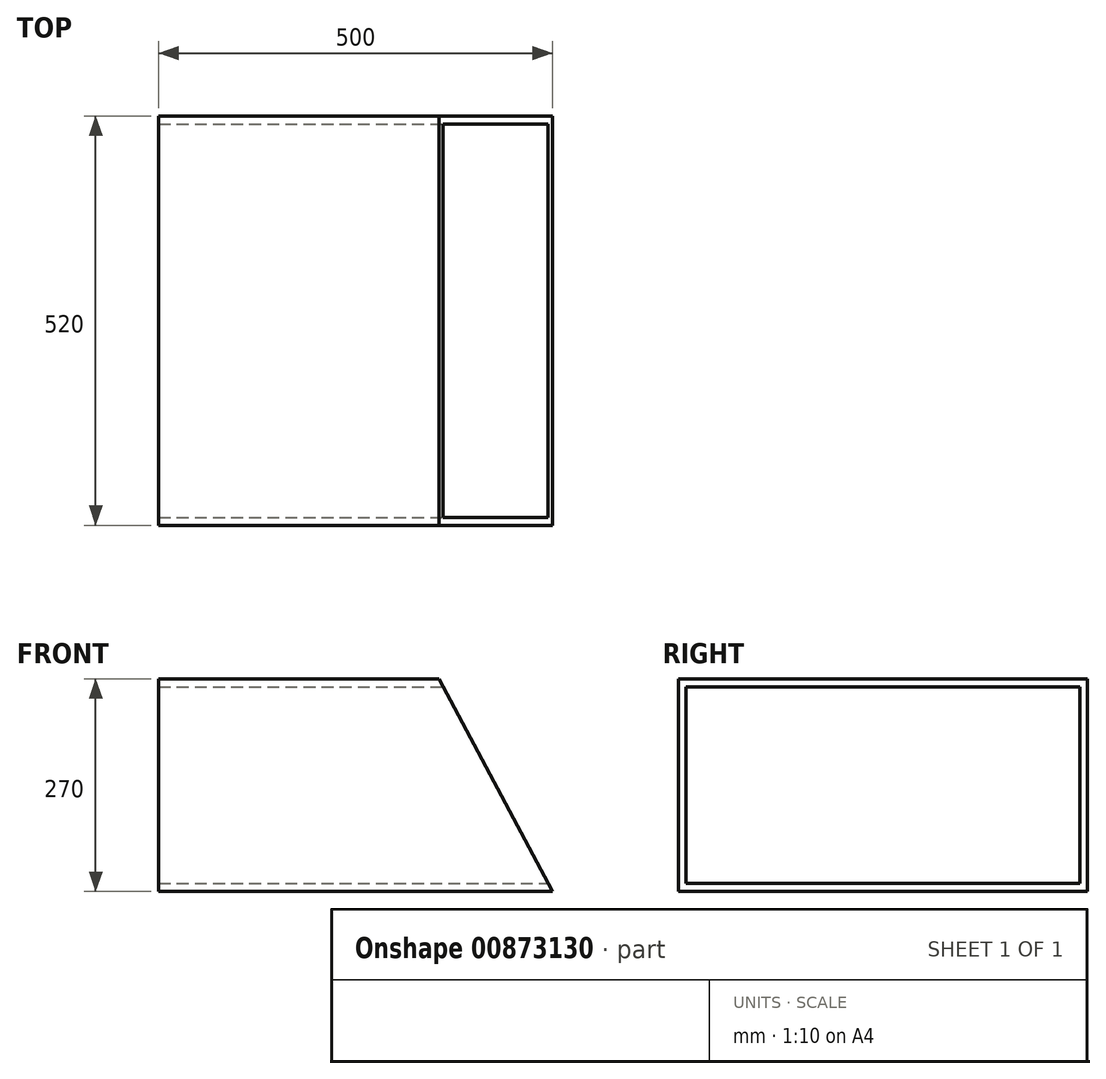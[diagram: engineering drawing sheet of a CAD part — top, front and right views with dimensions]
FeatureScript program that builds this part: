
annotation { "Feature Type Name" : "Feature", "Feature Type Description" : "" }
export const myFeature = defineFeature(function(context is Context, id is Id, definition is map)
    precondition{}
    {
        {
            var Q0;
            Q0=qCreatedBy(makeId("Right.planeOp"),FACE);
            var sketch = newSketch(context, id + "F0", { "sketchPlane" : qUnion([Q0])});
            skLineSegment(sketch, "E0.bottom", {"start": v(260, -135) * mm, "end": v(-260, -135) * mm});
            skLineSegment(sketch, "E0.top", {"start": v(260, 135) * mm, "end": v(-260, 135) * mm});
            skLineSegment(sketch, "E0.left", {"start": v(260, -135) * mm, "end": v(260, 135) * mm});
            skLineSegment(sketch, "E0.right", {"start": v(-260, -135) * mm, "end": v(-260, 135) * mm});
            skPoint(sketch, "E0.middle", {"position": v(0, 0) * mm});
            skSolve(sketch);
        }
        {
            var Q0;
            Q0=makeQuery(id+"F0.imprint","IMPRINT",FACE,{"disambiguationData":[TD([[makeQuery(id+"F0.imprint","IMPRINT",EDGE,{"derivedFrom":sQuery(id+"F0.wireOp",EDGE,"E0.bottom")}),-1.0]])]});
            extrude(context, id + "F1", {"entities" : qUnion([Q0]), "oppositeDirection" : true, "depth" : 500 * mm, "offsetDistance" : 25 * mm});
        }
        {
            var Q0;
            Q0=makeQuery(id+"F1.opExtrude","CAP_FACE",FACE,{"disambiguationData":[OSD([sQuery(id+"F0.wireOp",EDGE,"E0.bottom"),sQuery(id+"F0.wireOp",EDGE,"E0.top"),sQuery(id+"F0.wireOp",EDGE,"E0.left"),sQuery(id+"F0.wireOp",EDGE,"E0.right")])],"isStart":true});
            var sketch = newSketch(context, id + "F2", { "sketchPlane" : qUnion([Q0])});
            skLineSegment(sketch, "E1.bottom", {"start": v(250, -125) * mm, "end": v(-250, -125) * mm});
            skLineSegment(sketch, "E1.top", {"start": v(250, 125) * mm, "end": v(-250, 125) * mm});
            skLineSegment(sketch, "E1.left", {"start": v(250, -125) * mm, "end": v(250, 125) * mm});
            skLineSegment(sketch, "E1.right", {"start": v(-250, -125) * mm, "end": v(-250, 125) * mm});
            skPoint(sketch, "E1.middle", {"position": v(0, 0) * mm});
            skSolve(sketch);
        }
        {
            var Q0;
            Q0=makeQuery(id+"F2.imprint","IMPRINT",FACE,{"disambiguationData":[TD([[makeQuery(id+"F2.imprint","IMPRINT",EDGE,{"derivedFrom":sQuery(id+"F2.wireOp",EDGE,"E1.bottom")}),-1.0]])]});
            extrude(context, id + "F3", {"entities" : qUnion([Q0]), "operationType" : NewBodyOperationType.REMOVE, "oppositeDirection" : true, "depth" : 500 * mm, "offsetDistance" : 25 * mm});
        }
        {
            var Q0;
            Q0=makeQuery(id+"F1.opExtrude","SWEPT_FACE",FACE,{"disambiguationData":[OSD([sQuery(id+"F0.wireOp",EDGE,"E0.right")])]});
            var sketch = newSketch(context, id + "F4", { "sketchPlane" : qUnion([Q0])});
            skLineSegment(sketch, "E2", {"start": v(0, -135) * mm, "end": v(-144.17, 135) * mm});
            skLineSegment(sketch, "E3", {"start": v(-144.17, 135) * mm, "end": v(0, 135) * mm});
            skLineSegment(sketch, "E4", {"start": v(0, 135) * mm, "end": v(0, -135) * mm});
            skSolve(sketch);
        }
        {
            var Q0;
            Q0=makeQuery(id+"F4.imprint","IMPRINT",FACE,{"disambiguationData":[TD([[makeQuery(id+"F4.imprint","IMPRINT",EDGE,{"derivedFrom":sQuery(id+"F4.wireOp",EDGE,"E2")}),-1.0]])]});
            extrude(context, id + "F5", {"entities" : qUnion([Q0]), "operationType" : NewBodyOperationType.REMOVE, "oppositeDirection" : true, "depth" : 600 * mm, "offsetDistance" : 25 * mm});
        }
    });
